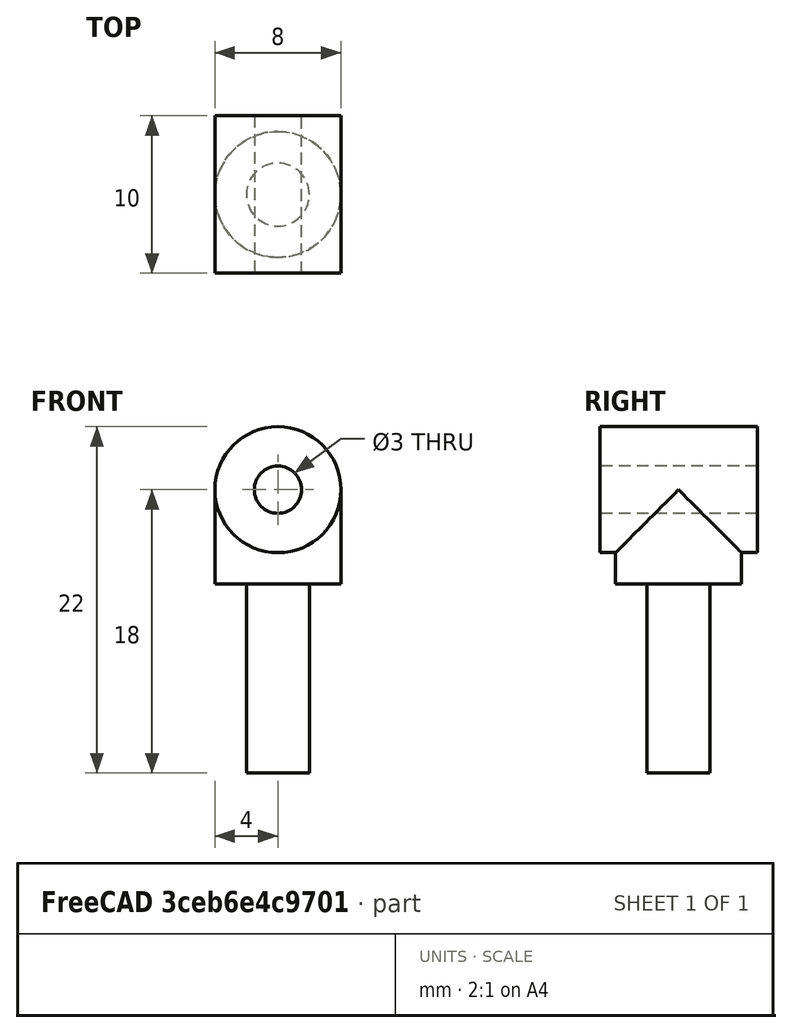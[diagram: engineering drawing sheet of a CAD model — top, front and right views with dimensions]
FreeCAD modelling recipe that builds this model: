
FCSTD DOCUMENT  (FreeCAD 0.20R29177 +426 (Git))
Label: daempfer-feder-kolben
License: All rights reserved
LicenseURL: http://en.wikipedia.org/wiki/All_rights_reserved
objects: TechDraw::DrawViewDimension×7, Sketcher::SketchObject×3, TechDraw::DrawProjGroupItem×3, PartDesign::Plane×1, PartDesign::Revolution×1, PartDesign::Pad×1, PartDesign::Pocket×1, PartDesign::Body×1, TechDraw::DrawSVGTemplate×1, TechDraw::DrawProjGroup×1, TechDraw::DrawPage×1
note: 11 computed .brp shape members not serialized (recipe doc carries the construction recipe); baked Part::Feature solids carry a one-line shape summary decoded from their .brp

FEATURE [PartDesign::Plane] DatumPlane
  Length = 60
  MapMode = 5
  Placement = pos=(0,0,0) rot=(1,0,0;1.5708rad)
  ResizeMode = 0
  Support = -> [XZ_Plane]
  Width = 60
FEATURE [Sketcher::SketchObject] Sketch
  FullyConstrained = true
  MapMode = 5
  Placement = pos=(0,0,0) rot=(1,0,0;1.5708rad)
  Support = -> [DatumPlane]
  sketch-geometry (6):
    g0: LineSegment StartX=0 StartY=0 StartZ=0 EndX=2 EndY=0 EndZ=0
    g1: LineSegment StartX=2 StartY=0 StartZ=0 EndX=2 EndY=12 EndZ=0
    g2: LineSegment StartX=0 StartY=18 StartZ=0 EndX=0 EndY=0 EndZ=0
    g3: LineSegment StartX=0 StartY=18 StartZ=0 EndX=4 EndY=18 EndZ=0
    g4: LineSegment StartX=4 StartY=18 StartZ=0 EndX=4 EndY=12 EndZ=0
    g5: LineSegment StartX=4 StartY=12 StartZ=0 EndX=2 EndY=12 EndZ=0
  constraints (17):
    c: Coincident(g0,g1)
    c: Coincident(g2,g0)
    c: Horizontal(g0)
    c: Vertical(g1)
    c: Vertical(g2)
    c: Coincident(g0,g-1)
    c: DistanceY(g1,g1) = 12
    c: DistanceX(g2,g1) = 2
    c: Coincident(g2,g3)
    c: Horizontal(g3)
    c: Coincident(g3,g4)
    c: Vertical(g4)
    c: Coincident(g4,g5)
    c: Coincident(g5,g1)
    c: Horizontal(g5)
    c: DistanceX(g2,g3) = 4
    c: DistanceY(g4,g4) = 6
FEATURE [PartDesign::Revolution] Revolution
  Angle = 360
  Axis = (0,-2e-16,1)
  Base = (0,0,0)
  Placement = pos=(0,0,0) rot=(1,0,0;1.5708rad)
  Profile = -> Sketch
  ReferenceAxis = -> Sketch [V_Axis]
  Reversed = true
FEATURE [Sketcher::SketchObject] Sketch001
  FullyConstrained = true
  MapMode = 5
  Placement = pos=(0,0,0) rot=(1,0,0;1.5708rad)
  Support = -> [DatumPlane]
  sketch-geometry (1):
    g0: Circle CenterX=0 CenterY=18 CenterZ=0 NormalX=0 NormalY=0 NormalZ=1 AngleXU=0 Radius=4
  constraints (3):
    c: PointOnObject(g0,g-2)
    c: Radius(g0) = 4
    c: DistanceY(g-1,g0) = 18
FEATURE [PartDesign::Pad] Pad
  BaseFeature = -> Revolution
  Direction = (1,1,1)
  Length = 10
  Length2 = 100
  Midplane = true
  Placement = pos=(0,0,0) rot=(1,0,0;1.5708rad)
  Profile = -> Sketch001
  Type = 0
FEATURE [Sketcher::SketchObject] Sketch002
  FullyConstrained = true
  MapMode = 5
  Placement = pos=(0,0,0) rot=(1,0,0;1.5708rad)
  Support = -> [DatumPlane]
  sketch-geometry (1):
    g0: Circle CenterX=0 CenterY=18 CenterZ=0 NormalX=0 NormalY=0 NormalZ=1 AngleXU=0 Radius=1.5
  constraints (3):
    c: PointOnObject(g0,g-2)
    c: DistanceY(g-1,g0) = 18
    c: Radius(g0) = 1.5
FEATURE [PartDesign::Pocket] Pocket
  BaseFeature = -> Pad
  Direction = (1,1,1)
  Length = 5
  Length2 = 100
  Midplane = true
  Placement = pos=(0,0,0) rot=(1,0,0;1.5708rad)
  Profile = -> Sketch002
  Type = 1
FEATURE [PartDesign::Body] Body
  Group = -> [DatumPlane,Sketch,Revolution,Sketch001,Pad,Sketch002,Pocket]
  Origin = -> Origin
  Tip = -> Pocket
FEATURE [TechDraw::DrawSVGTemplate] Template
  EditableTexts = Designed_by_Name=Aleksander Sadowski; FC-SC=4:1; FC-Title=damper piston; Subtitle=Mars Rover
  Height = 210
  Orientation = 1
  Width = 297
FEATURE [TechDraw::DrawProjGroupItem] ProjItem  label="Front"
  CoarseView = false
  Direction = (0,-1,0)
  Focus = 100
  HardHidden = false
  IsoCount = 0
  IsoHidden = false
  IsoVisible = false
  LockPosition = true
  Perspective = false
  Rotation = 0
  RotationVector = (1,0,0)
  Scale = 4
  ScaleType = 2
  SeamHidden = false
  SeamVisible = true
  SmoothHidden = false
  SmoothVisible = true
  Source = -> [Body]
  Type = 0
  X = 0
  XDirection = (1,0,0)
  Y = 0
FEATURE [TechDraw::DrawProjGroupItem] ProjItem001  label="Left"
  CoarseView = false
  Direction = (-1,-1e-16,0)
  Focus = 100
  HardHidden = false
  IsoCount = 0
  IsoHidden = false
  IsoVisible = false
  LockPosition = false
  Perspective = false
  Rotation = 0
  RotationVector = (1,0,0)
  Scale = 4
  ScaleType = 2
  SeamHidden = false
  SeamVisible = true
  SmoothHidden = false
  SmoothVisible = true
  Source = -> [Body]
  Type = 1
  X = 82.9337
  XDirection = (1e-16,-1,0)
  Y = 0
FEATURE [TechDraw::DrawProjGroupItem] ProjItem002  label="FrontTopLeft"
  CoarseView = false
  Direction = (-0.57735,-0.57735,0.57735)
  Focus = 100
  HardHidden = false
  IsoCount = 0
  IsoHidden = false
  IsoVisible = false
  LockPosition = false
  Perspective = false
  Rotation = 0
  RotationVector = (1,0,0)
  Scale = 4
  ScaleType = 2
  SeamHidden = false
  SeamVisible = true
  SmoothHidden = false
  SmoothVisible = true
  Source = -> [Body]
  Type = 6
  X = 160.69
  XDirection = (0.707107,-0.707107,0)
  Y = 1.92979
FEATURE [TechDraw::DrawProjGroup] ProjGroup
  Anchor = -> ProjItem
  AutoDistribute = true
  LockPosition = false
  ProjectionType = 0
  Rotation = 0
  Scale = 4
  ScaleType = 2
  Source = -> [Body]
  Views = -> [ProjItem,ProjItem001,ProjItem002]
  X = 66.6839
  Y = 126.375
  spacingX = 15
  spacingY = 15
FEATURE [TechDraw::DrawViewDimension] Dimension
  AngleOverride = false
  Arbitrary = false
  ArbitraryTolerances = false
  EqualTolerance = true
  ExtensionAngle = 0
  FormatSpec = %.0f
  FormatSpecOverTolerance = %+.2f
  FormatSpecUnderTolerance = %+.2f
  Inverted = false
  LineAngle = 0
  LockPosition = false
  MeasureType = 1
  OverTolerance = 0
  References2D = -> [ProjItem001]
  Rotation = 0
  ScaleType = 0
  TheoreticalExact = false
  Type = 1
  UnderTolerance = 0
  X = 0
  Y = 54.5926
FEATURE [TechDraw::DrawViewDimension] Dimension001
  AngleOverride = false
  Arbitrary = false
  ArbitraryTolerances = false
  EqualTolerance = true
  ExtensionAngle = 0
  FormatSpec = ⌀ %.0f
  FormatSpecOverTolerance = %+.2f
  FormatSpecUnderTolerance = %+.2f
  Inverted = false
  LineAngle = 0
  LockPosition = false
  MeasureType = 1
  OverTolerance = 0
  References2D = -> [ProjItem]
  Rotation = 0
  ScaleType = 0
  TheoreticalExact = false
  Type = 5
  UnderTolerance = 0
  X = 16.5048
  Y = 52.2241
FEATURE [TechDraw::DrawViewDimension] Dimension002
  AngleOverride = false
  Arbitrary = false
  ArbitraryTolerances = false
  EqualTolerance = true
  ExtensionAngle = 0
  FormatSpec = ⌀ %.0f
  FormatSpecOverTolerance = %+.2f
  FormatSpecUnderTolerance = %+.2f
  Inverted = false
  LineAngle = 0
  LockPosition = false
  MeasureType = 1
  OverTolerance = 0
  References2D = -> [ProjItem]
  Rotation = 0
  ScaleType = 0
  TheoreticalExact = false
  Type = 5
  UnderTolerance = 0
  X = 26.8511
  Y = 47.051
FEATURE [TechDraw::DrawViewDimension] Dimension003
  AngleOverride = false
  Arbitrary = false
  ArbitraryTolerances = false
  EqualTolerance = true
  ExtensionAngle = 0
  FormatSpec = %.0f
  FormatSpecOverTolerance = %+.2f
  FormatSpecUnderTolerance = %+.2f
  Inverted = false
  LineAngle = 0
  LockPosition = false
  MeasureType = 1
  OverTolerance = 0
  References2D = -> [ProjItem]
  Rotation = 0
  ScaleType = 0
  TheoreticalExact = false
  Type = 2
  UnderTolerance = 0
  X = 22.5341
  Y = -20
FEATURE [TechDraw::DrawViewDimension] Dimension004
  AngleOverride = false
  Arbitrary = false
  ArbitraryTolerances = false
  EqualTolerance = true
  ExtensionAngle = 0
  FormatSpec = %.0f
  FormatSpecOverTolerance = %+.2f
  FormatSpecUnderTolerance = %+.2f
  Inverted = false
  LineAngle = 0
  LockPosition = false
  MeasureType = 1
  OverTolerance = 0
  References2D = -> [ProjItem]
  Rotation = 0
  ScaleType = 0
  TheoreticalExact = false
  Type = 2
  UnderTolerance = 0
  X = 31.895
  Y = -6.7683
FEATURE [TechDraw::DrawViewDimension] Dimension005
  AngleOverride = false
  Arbitrary = false
  ArbitraryTolerances = false
  EqualTolerance = true
  ExtensionAngle = 0
  FormatSpec = ⌀ %.0f
  FormatSpecOverTolerance = %+.2f
  FormatSpecUnderTolerance = %+.2f
  Inverted = false
  LineAngle = 0
  LockPosition = false
  MeasureType = 1
  OverTolerance = 0
  References2D = -> [ProjItem]
  Rotation = 0
  ScaleType = 0
  TheoreticalExact = false
  Type = 1
  UnderTolerance = 0
  X = -1.12643
  Y = -51.4677
FEATURE [TechDraw::DrawViewDimension] Dimension006
  AngleOverride = false
  Arbitrary = false
  ArbitraryTolerances = false
  EqualTolerance = true
  ExtensionAngle = 0
  FormatSpec = ⌀ %.0f
  FormatSpecOverTolerance = %+.2f
  FormatSpecUnderTolerance = %+.2f
  Inverted = false
  LineAngle = 0
  LockPosition = false
  MeasureType = 1
  OverTolerance = 0
  References2D = -> [ProjItem]
  Rotation = 0
  ScaleType = 0
  TheoreticalExact = false
  Type = 1
  UnderTolerance = 0
  X = 0
  Y = -60.2948
FEATURE [TechDraw::DrawPage] Page
  KeepUpdated = true
  NextBalloonIndex = 1
  ProjectionType = 0
  Template = -> Template
  Views = -> [ProjGroup,Dimension,Dimension001,Dimension002,Dimension003,Dimension004,Dimension005,Dimension006]
